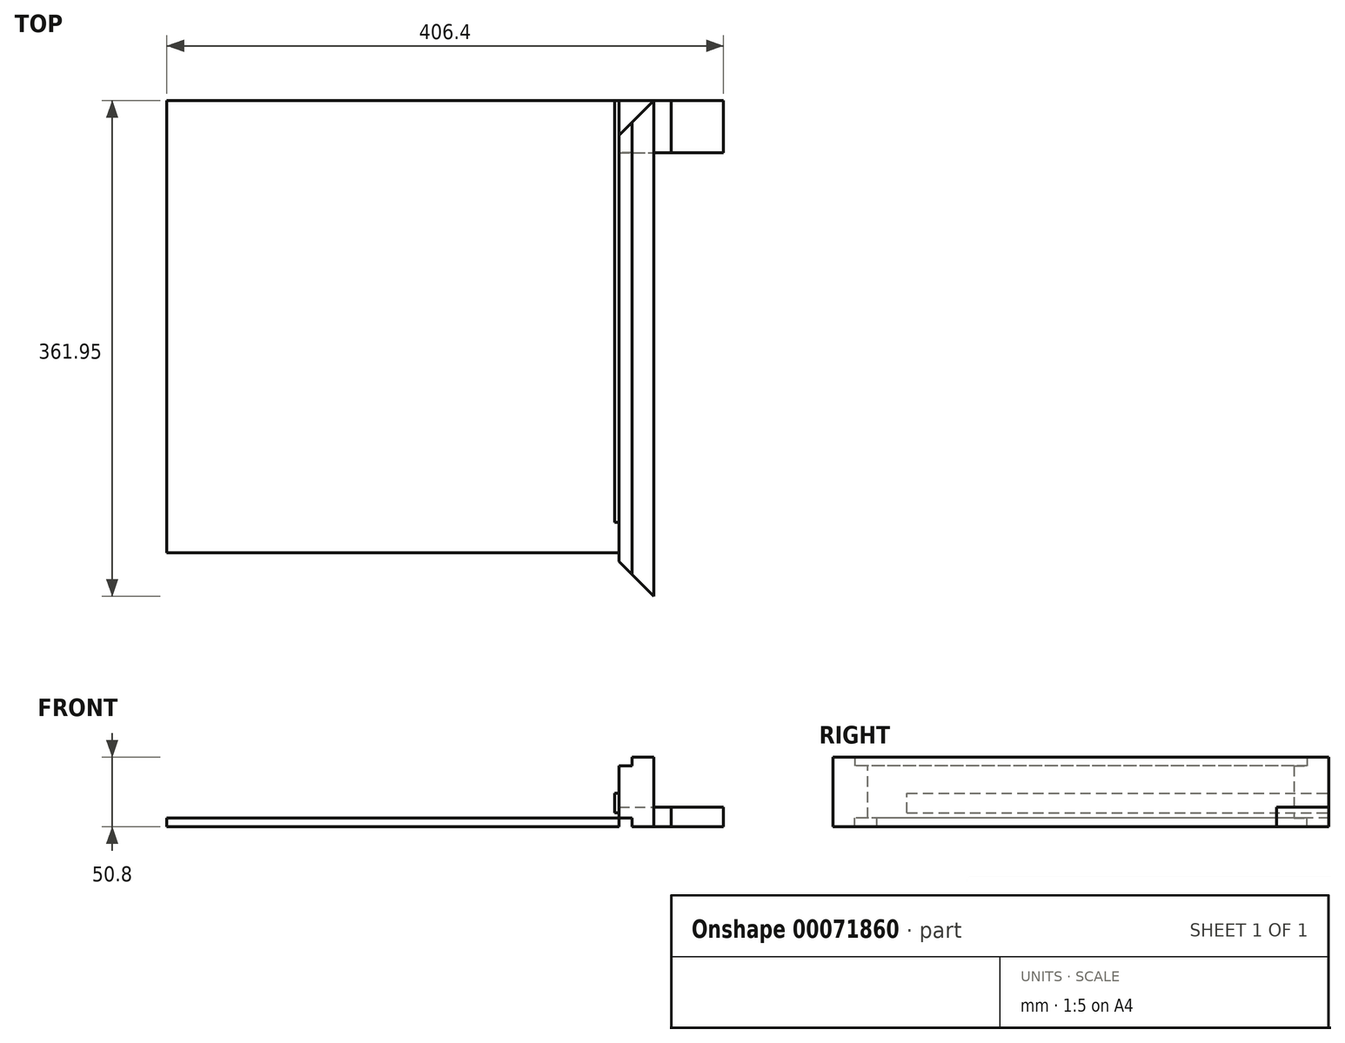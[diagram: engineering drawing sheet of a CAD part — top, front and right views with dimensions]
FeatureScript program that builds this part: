
annotation { "Feature Type Name" : "Feature", "Feature Type Description" : "" }
export const myFeature = defineFeature(function(context is Context, id is Id, definition is map)
    precondition{}
    {
        {
            var Q0;
            Q0=qCreatedBy(makeId("Top.planeOp"),FACE);
            var sketch = newSketch(context, id + "F0", { "sketchPlane" : qUnion([Q0])});
            skLineSegment(sketch, "E0.bottom", {"start": v(-330.2, 0) * mm, "end": v(0, 0) * mm});
            skLineSegment(sketch, "E0.top", {"start": v(-330.2, -330.2) * mm, "end": v(0, -330.2) * mm});
            skLineSegment(sketch, "E0.left", {"start": v(-330.2, 0) * mm, "end": v(-330.2, -330.2) * mm});
            skLineSegment(sketch, "E0.right", {"start": v(0, 0) * mm, "end": v(0, -330.2) * mm});
            skSolve(sketch);
        }
        {
            var Q0;
            Q0=qCreatedBy(makeId("Front.planeOp"),FACE);
            var sketch = newSketch(context, id + "F1", { "sketchPlane" : qUnion([Q0])});
            skLineSegment(sketch, "E1.bottom", {"start": v(0, 50.8) * mm, "end": v(25.4, 50.8) * mm});
            skLineSegment(sketch, "E1.top", {"start": v(0, 0) * mm, "end": v(25.4, 0) * mm});
            skLineSegment(sketch, "E1.left", {"start": v(0, 50.8) * mm, "end": v(0, 0) * mm});
            skLineSegment(sketch, "E1.right", {"start": v(25.4, 50.8) * mm, "end": v(25.4, 0) * mm});
            skSolve(sketch);
        }
        {
            var Q0;
            Q0=qCreatedBy(makeId("Top.planeOp"),FACE);
            var sketch = newSketch(context, id + "F2", { "sketchPlane" : qUnion([Q0])});
            skLineSegment(sketch, "E2.bottom", {"start": v(0, 0) * mm, "end": v(38.1, 0) * mm});
            skLineSegment(sketch, "E2.top", {"start": v(0, -38.1) * mm, "end": v(38.1, -38.1) * mm});
            skLineSegment(sketch, "E2.left", {"start": v(0, 0) * mm, "end": v(0, -38.1) * mm});
            skLineSegment(sketch, "E2.right", {"start": v(38.1, 0) * mm, "end": v(38.1, -38.1) * mm});
            skSolve(sketch);
        }
        {
            var Q0;
            Q0=makeQuery(id+"F0.imprint","IMPRINT",FACE,{"disambiguationData":[TD([[makeQuery(id+"F0.imprint","IMPRINT",EDGE,{"derivedFrom":sQuery(id+"F0.wireOp",EDGE,"E0.bottom")}),-1.0]])]});
            extrude(context, id + "F3", {"entities" : qUnion([Q0]), "depth" : 6.35 * mm});
        }
        {
            var Q0;
            Q0=makeQuery(id+"F2.imprint","IMPRINT",FACE,{"disambiguationData":[TD([[makeQuery(id+"F2.imprint","IMPRINT",EDGE,{"derivedFrom":sQuery(id+"F2.wireOp",EDGE,"E2.bottom")}),-1.0]])]});
            extrude(context, id + "F4", {"entities" : qUnion([Q0]), "depth" : 14.29 * mm});
        }
        {
            var Q0;
            Q0=makeQuery(id+"F1.imprint","IMPRINT",FACE,{"disambiguationData":[TD([[makeQuery(id+"F1.imprint","IMPRINT",EDGE,{"derivedFrom":sQuery(id+"F1.wireOp",EDGE,"E1.bottom")}),-1.0]])]});
            extrude(context, id + "F5", {"entities" : qUnion([Q0]), "depth" : 361.95 * mm});
        }
        {
            var Q0;
            Q0=makeQuery(id+"F5.opExtrude","CAP_FACE",FACE,{"disambiguationData":[OSD([sQuery(id+"F1.wireOp",EDGE,"E1.bottom"),sQuery(id+"F1.wireOp",EDGE,"E1.top"),sQuery(id+"F1.wireOp",EDGE,"E1.left"),sQuery(id+"F1.wireOp",EDGE,"E1.right")])],"isStart":false});
            var sketch = newSketch(context, id + "F6", { "sketchPlane" : qUnion([Q0])});
            skLineSegment(sketch, "E3.bottom", {"start": v(0, 50.8) * mm, "end": v(9.52, 50.8) * mm});
            skLineSegment(sketch, "E3.top", {"start": v(0, 44.45) * mm, "end": v(9.52, 44.45) * mm});
            skLineSegment(sketch, "E3.left", {"start": v(0, 50.8) * mm, "end": v(0, 44.45) * mm});
            skLineSegment(sketch, "E3.right", {"start": v(9.52, 50.8) * mm, "end": v(9.52, 44.45) * mm});
            skLineSegment(sketch, "E4.bottom", {"start": v(0, 0) * mm, "end": v(9.52, 0) * mm});
            skLineSegment(sketch, "E4.top", {"start": v(0, 6.35) * mm, "end": v(9.52, 6.35) * mm});
            skLineSegment(sketch, "E4.left", {"start": v(0, 0) * mm, "end": v(0, 6.35) * mm});
            skLineSegment(sketch, "E4.right", {"start": v(9.52, 0) * mm, "end": v(9.52, 6.35) * mm});
            skSolve(sketch);
        }
        {
            var Q0;
            Q0=qCreatedBy(makeId("Front.planeOp"),FACE);
            var sketch = newSketch(context, id + "F7", { "sketchPlane" : qUnion([Q0])});
            skLineSegment(sketch, "E5.bottom", {"start": v(0, 10.12) * mm, "end": v(-3.17, 10.12) * mm});
            skLineSegment(sketch, "E5.top", {"start": v(0, 24.4) * mm, "end": v(-3.18, 24.4) * mm});
            skLineSegment(sketch, "E5.left", {"start": v(0, 10.12) * mm, "end": v(0, 24.4) * mm});
            skLineSegment(sketch, "E5.right", {"start": v(-3.18, 10.12) * mm, "end": v(-3.18, 24.4) * mm});
            skSolve(sketch);
        }
        {
            var Q0;
            Q0=makeQuery(id+"F5.opExtrude","CAP_EDGE",EDGE,{"disambiguationData":[OSD([sQuery(id+"F1.wireOp",EDGE,"E1.left")])],"isStart":false});
            var Q1;
            Q1=makeQuery(id+"F5.opExtrude","CAP_EDGE",EDGE,{"disambiguationData":[OSD([sQuery(id+"F1.wireOp",EDGE,"E1.left")])],"isStart":true});
            chamfer(context, id + "F8", {"entities" : qUnion([Q0, Q1]), "width" : 25.4 * mm, "tangentPropagation" : true});
        }
        {
            var Q0;
            Q0 = qSketchRegion(id + "F6", true);
            extrude(context, id + "F9", {"entities" : qUnion([Q0]), "operationType" : NewBodyOperationType.REMOVE, "endBound" : BoundingType.THROUGH_ALL, "oppositeDirection" : true, "depth" : 406.4 * mm});
        }
        {
            var Q0;
            Q0 = qSketchRegion(id + "F7", true);
            extrude(context, id + "F10", {"entities" : qUnion([Q0]), "depth" : 307.97 * mm});
        }
        {
            var Q0;
            Q0=qCreatedBy(makeId("Top.planeOp"),FACE);
            var sketch = newSketch(context, id + "F11", { "sketchPlane" : qUnion([Q0])});
            skLineSegment(sketch, "E6.bottom", {"start": v(38.1, 0) * mm, "end": v(76.2, 0) * mm});
            skLineSegment(sketch, "E6.top", {"start": v(38.1, -38.1) * mm, "end": v(76.2, -38.1) * mm});
            skLineSegment(sketch, "E6.left", {"start": v(38.1, 0) * mm, "end": v(38.1, -38.1) * mm});
            skLineSegment(sketch, "E6.right", {"start": v(76.2, 0) * mm, "end": v(76.2, -38.1) * mm});
            skSolve(sketch);
        }
        {
            var Q0;
            Q0 = qSketchRegion(id + "F11", true);
            extrude(context, id + "F12", {"entities" : qUnion([Q0]), "depth" : 14.29 * mm});
        }
    });
